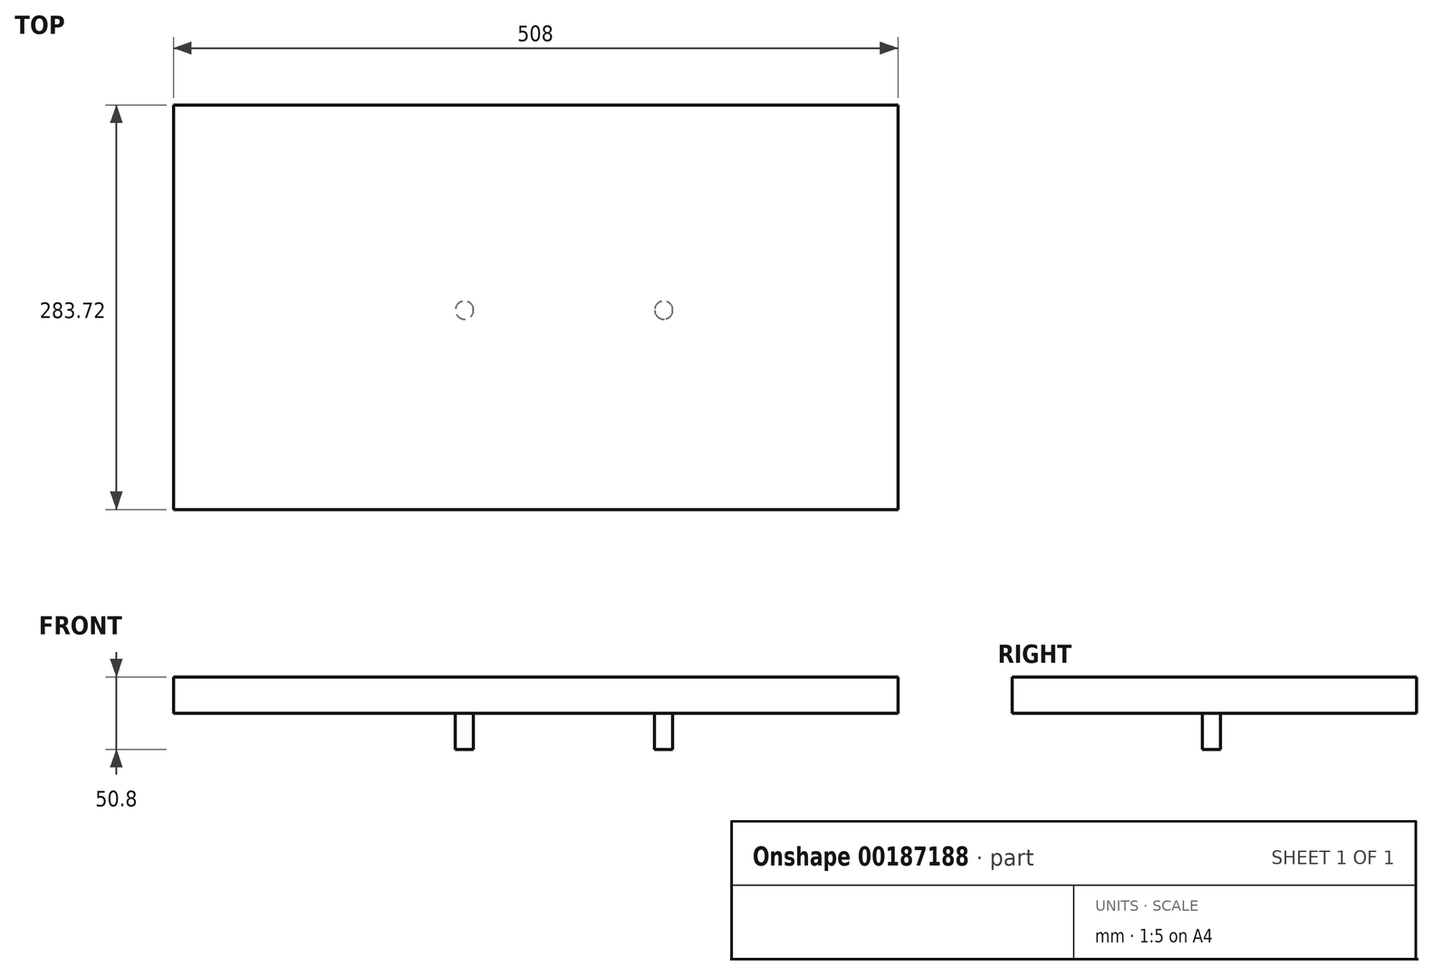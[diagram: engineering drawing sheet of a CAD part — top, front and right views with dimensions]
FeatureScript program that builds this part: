
annotation { "Feature Type Name" : "Feature", "Feature Type Description" : "" }
export const myFeature = defineFeature(function(context is Context, id is Id, definition is map)
    precondition{}
    {
        {
            var Q0;
            Q0=qCreatedBy(makeId("Top.planeOp"),FACE);
            var sketch = newSketch(context, id + "F0", { "sketchPlane" : qUnion([Q0])});
            skLineSegment(sketch, "E0.bottom", {"start": v(-245.36, -139.92) * mm, "end": v(262.64, -139.92) * mm});
            skLineSegment(sketch, "E0.top", {"start": v(-245.36, 143.8) * mm, "end": v(262.64, 143.8) * mm});
            skLineSegment(sketch, "E0.left", {"start": v(-245.36, -139.92) * mm, "end": v(-245.36, 143.8) * mm});
            skLineSegment(sketch, "E0.right", {"start": v(262.64, -139.92) * mm, "end": v(262.64, 143.8) * mm});
            skSolve(sketch);
        }
        {
            var Q0;
            Q0 = qSketchRegion(id + "F0", true);
            extrude(context, id + "F1", {"entities" : qUnion([Q0]), "depth" : 25.4 * mm});
        }
        {
            var Q0;
            Q0=makeQuery(id+"F1.opExtrude","CAP_FACE",FACE,{"disambiguationData":[OSD([sQuery(id+"F0.wireOp",EDGE,"E0.bottom"),sQuery(id+"F0.wireOp",EDGE,"E0.top"),sQuery(id+"F0.wireOp",EDGE,"E0.left"),sQuery(id+"F0.wireOp",EDGE,"E0.right")])],"isStart":true});
            var sketch = newSketch(context, id + "F2", { "sketchPlane" : qUnion([Q0])});
            skCircle(sketch, "E1", {"center": v(-41.29, 0) * mm, "radius": 6.35 * mm});
            skCircle(sketch, "E2", {"center": v(98.41, 0) * mm, "radius": 6.35 * mm});
            skSolve(sketch);
        }
        {
            var Q0;
            Q0=makeQuery(id+"F2.imprint","IMPRINT",FACE,{"disambiguationData":[TD([[makeQuery(id+"F2.imprint","IMPRINT",EDGE,{"derivedFrom":sQuery(id+"F2.wireOp",EDGE,"E1")}),1.0]])]});
            var Q1;
            Q1=makeQuery(id+"F2.imprint","IMPRINT",FACE,{"disambiguationData":[TD([[makeQuery(id+"F2.imprint","IMPRINT",EDGE,{"derivedFrom":sQuery(id+"F2.wireOp",EDGE,"E2")}),1.0]])]});
            extrude(context, id + "F3", {"entities" : qUnion([Q0, Q1]), "operationType" : NewBodyOperationType.ADD, "depth" : 25.4 * mm});
        }
    });
